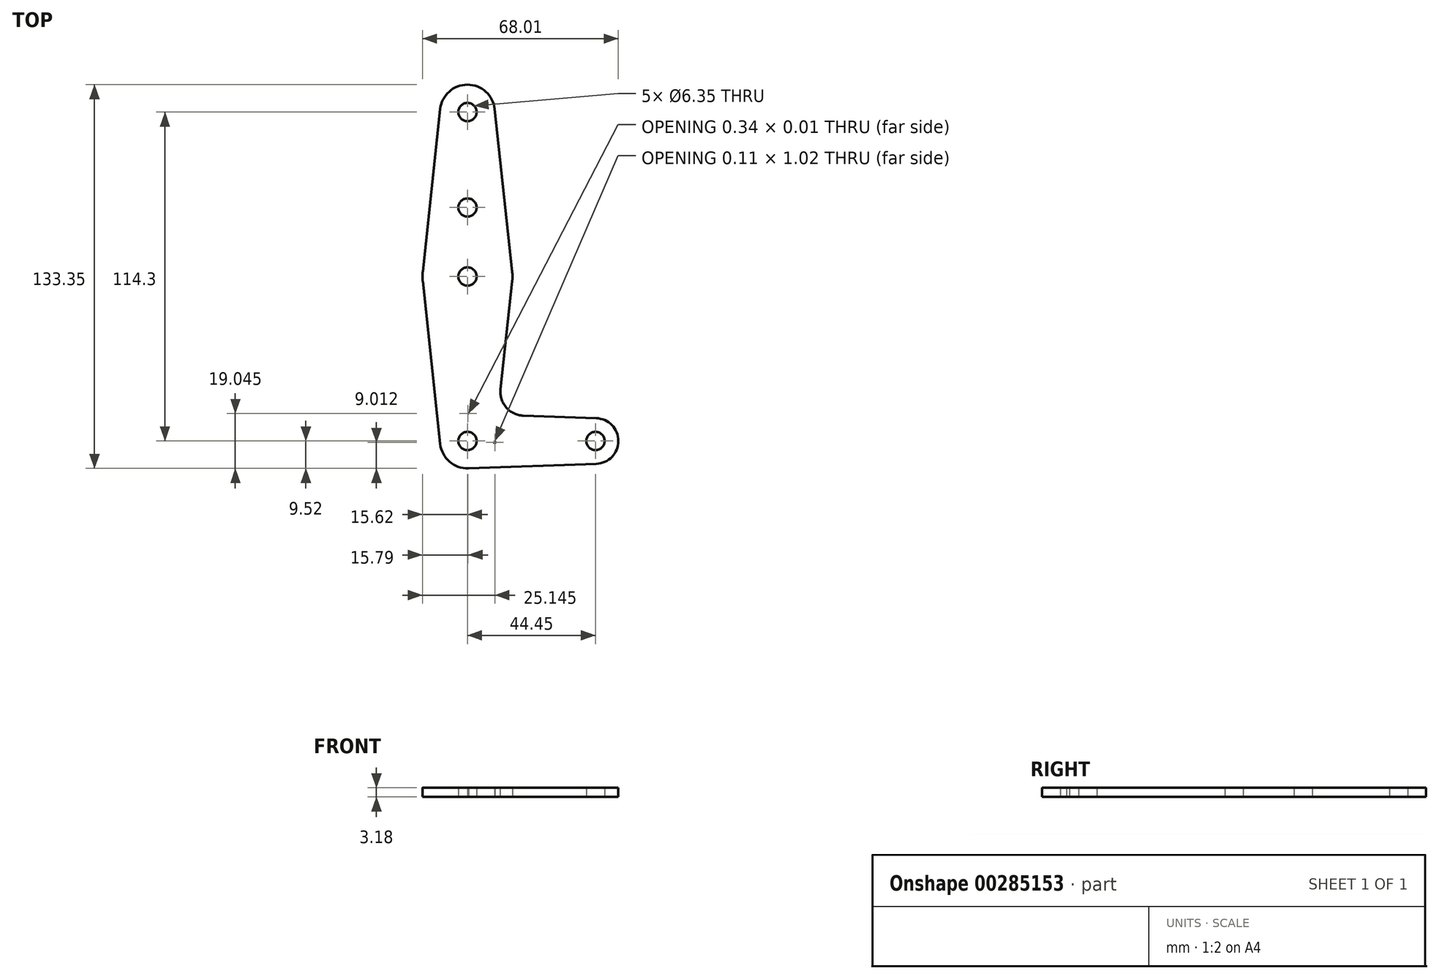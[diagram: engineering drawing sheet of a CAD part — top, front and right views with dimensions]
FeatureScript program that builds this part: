
annotation { "Feature Type Name" : "Feature", "Feature Type Description" : "" }
export const myFeature = defineFeature(function(context is Context, id is Id, definition is map)
    precondition{}
    {
        {
            var Q0;
            Q0=qCreatedBy(makeId("Top.planeOp"),FACE);
            var sketch = newSketch(context, id + "F0", { "sketchPlane" : qUnion([Q0])});
            skCircle(sketch, "E0", {"center": v(0, 0) * mm, "radius": 3.18 * mm});
            skCircle(sketch, "E1", {"center": v(0, 114.3) * mm, "radius": 3.18 * mm});
            skCircle(sketch, "E2", {"center": v(44.45, 0) * mm, "radius": 3.18 * mm});
            skLineSegment(sketch, "E3", {"start": v(0, 0) * mm, "end": v(44.45, 0) * mm});
            skLineSegment(sketch, "E4", {"start": v(0, 0) * mm, "end": v(0, 114.3) * mm});
            skCircle(sketch, "E5", {"center": v(0, 57.15) * mm, "radius": 3.18 * mm});
            skCircle(sketch, "E6", {"center": v(0, 81.14) * mm, "radius": 3.18 * mm});
            skCircle(sketch, "E7", {"center": v(0, 114.3) * mm, "radius": 9.53 * mm});
            skCircle(sketch, "E8", {"center": v(0, 57.15) * mm, "radius": 15.62 * mm});
            skCircle(sketch, "E9", {"center": v(0, 0) * mm, "radius": 9.53 * mm});
            skCircle(sketch, "E10", {"center": v(44.45, 0) * mm, "radius": 7.94 * mm});
            skLineSegment(sketch, "E11", {"start": v(-15.53, 58.82) * mm, "end": v(-9.47, 115.32) * mm});
            skLineSegment(sketch, "E12", {"start": v(9.47, 115.32) * mm, "end": v(15.53, 58.82) * mm});
            skLineSegment(sketch, "E13", {"start": v(-15.53, 55.48) * mm, "end": v(-9.47, -1.02) * mm});
            skLineSegment(sketch, "E14", {"start": v(15.53, 55.48) * mm, "end": v(9.47, -1.02) * mm});
            skLineSegment(sketch, "E15.trimOffspring", {"start": v(0, 9.53) * mm, "end": v(44.73, 7.93) * mm});
            skLineSegment(sketch, "E16", {"start": v(0.34, -9.52) * mm, "end": v(44.73, -7.93) * mm});
            skSolve(sketch);
        }
        {
            var Q0;
            {var subQ0=sQuery(id+"F0.wireOp",EDGE,"E11");Q0=makeQuery(id+"F0.imprint","IMPRINT",FACE,{"disambiguationData":[TD([[makeQuery(id+"F0.imprint","IMPRINT",EDGE,{"derivedFrom":subQ0}),-1.0]])]});}
            var Q1;
            {var subQ0=sQuery(id+"F0.wireOp",EDGE,"E12");Q1=makeQuery(id+"F0.imprint","IMPRINT",FACE,{"disambiguationData":[TD([[makeQuery(id+"F0.imprint","IMPRINT",EDGE,{"derivedFrom":subQ0}),-1.0]])]});}
            var Q2;
            Q2=makeQuery(id+"F0.imprint","IMPRINT",FACE,{"disambiguationData":[TD([[makeQuery(id+"F0.imprint","IMPRINT",EDGE,{"derivedFrom":sQuery(id+"F0.wireOp",EDGE,"E1")}),-1.0]])]});
            var Q3;
            {var subQ0=sQuery(id+"F0.wireOp",EDGE,"E13");Q3=makeQuery(id+"F0.imprint","IMPRINT",FACE,{"disambiguationData":[TD([[makeQuery(id+"F0.imprint","IMPRINT",EDGE,{"derivedFrom":subQ0}),1.0]])]});}
            var Q4;
            {var subQ3=sQuery(id+"F0.wireOp",EDGE,"E15.trimOffspring");var subQ5=sQuery(id+"F0.wireOp",EDGE,"E4");var subQ7=makeQuery(id+"F0.imprint","INTERSECT",VERTEX,{"derivedFrom":[subQ5,subQ3]});Q4=makeQuery(id+"F0.imprint","IMPRINT",FACE,{"disambiguationData":[TD([[makeQuery(id+"F0.imprint","IMPRINT",EDGE,{"disambiguationData":[TD([[subQ7,-1.0]])],"derivedFrom":subQ5}),-1.0]])]});}
            var Q5;
            {var subQ0=sQuery(id+"F0.wireOp",EDGE,"E8");var subQ2=sQuery(id+"F0.wireOp",EDGE,"E4");var subQ8=makeQuery(id+"F0.imprint","INTERSECT",VERTEX,{"disambiguationData":[OD(0.0)],"derivedFrom":[subQ2,subQ0]});Q5=makeQuery(id+"F0.imprint","IMPRINT",FACE,{"disambiguationData":[TD([[makeQuery(id+"F0.imprint","IMPRINT",EDGE,{"disambiguationData":[TD([[subQ8,-1.0]])],"derivedFrom":subQ2}),-1.0]])]});}
            var Q6;
            {var subQ0=sQuery(id+"F0.wireOp",EDGE,"E8");var subQ2=sQuery(id+"F0.wireOp",EDGE,"E4");var subQ7=makeQuery(id+"F0.imprint","INTERSECT",VERTEX,{"disambiguationData":[OD(0.0)],"derivedFrom":[subQ2,subQ0]});Q6=makeQuery(id+"F0.imprint","IMPRINT",FACE,{"disambiguationData":[TD([[makeQuery(id+"F0.imprint","IMPRINT",EDGE,{"disambiguationData":[TD([[subQ7,-1.0]])],"derivedFrom":subQ2}),1.0]])]});}
            var Q7;
            {var subQ4=sQuery(id+"F0.wireOp",EDGE,"E0");var subQ6=sQuery(id+"F0.wireOp",EDGE,"E3");var subQ7=makeQuery(id+"F0.imprint","INTERSECT",VERTEX,{"derivedFrom":[subQ4,subQ6]});Q7=makeQuery(id+"F0.imprint","IMPRINT",FACE,{"disambiguationData":[TD([[makeQuery(id+"F0.imprint","IMPRINT",EDGE,{"disambiguationData":[TD([[subQ7,1.0]])],"derivedFrom":subQ4}),-1.0]])]});}
            var Q8;
            {var subQ1=sQuery(id+"F0.wireOp",EDGE,"E3");var subQ5=sQuery(id+"F0.wireOp",EDGE,"E0");var subQ8=makeQuery(id+"F0.imprint","INTERSECT",VERTEX,{"derivedFrom":[subQ5,subQ1]});Q8=makeQuery(id+"F0.imprint","IMPRINT",FACE,{"disambiguationData":[TD([[makeQuery(id+"F0.imprint","IMPRINT",EDGE,{"disambiguationData":[TD([[subQ8,-1.0]])],"derivedFrom":subQ5}),-1.0]])]});}
            var Q9;
            {var subQ0=sQuery(id+"F0.wireOp",EDGE,"E9");var subQ1=sQuery(id+"F0.wireOp",EDGE,"E3");var subQ2=makeQuery(id+"F0.imprint","INTERSECT",VERTEX,{"derivedFrom":[subQ1,subQ0]});Q9=makeQuery(id+"F0.imprint","IMPRINT",FACE,{"disambiguationData":[TD([[makeQuery(id+"F0.imprint","IMPRINT",EDGE,{"disambiguationData":[TD([[subQ2,-1.0]])],"derivedFrom":subQ1}),1.0]])]});}
            var Q10;
            {var subQ0=sQuery(id+"F0.wireOp",EDGE,"E10");var subQ1=sQuery(id+"F0.wireOp",EDGE,"E3");var subQ2=makeQuery(id+"F0.imprint","INTERSECT",VERTEX,{"derivedFrom":[subQ1,subQ0]});Q10=makeQuery(id+"F0.imprint","IMPRINT",FACE,{"disambiguationData":[TD([[makeQuery(id+"F0.imprint","IMPRINT",EDGE,{"disambiguationData":[TD([[subQ2,1.0]])],"derivedFrom":subQ1}),1.0]])]});}
            var Q11;
            {var subQ0=sQuery(id+"F0.wireOp",EDGE,"E16");Q11=makeQuery(id+"F0.imprint","IMPRINT",FACE,{"disambiguationData":[TD([[makeQuery(id+"F0.imprint","IMPRINT",EDGE,{"derivedFrom":subQ0}),1.0]])]});}
            var Q12;
            Q12=makeQuery(id+"F0.imprint","IMPRINT",FACE,{"disambiguationData":[TD([[makeQuery(id+"F0.imprint","IMPRINT",EDGE,{"derivedFrom":sQuery(id+"F0.wireOp",EDGE,"E2")}),-1.0]])]});
            extrude(context, id + "F1", {"entities" : qUnion([Q0, Q1, Q2, Q3, Q4, Q5, Q6, Q7, Q8, Q9, Q10, Q11, Q12]), "depth" : 3.17 * mm});
        }
        {
            var Q0;
            Q0=makeQuery(id+"F1.opExtrude","SWEPT_EDGE",EDGE,{"disambiguationData":[OSD([sQuery(id+"F0.wireOp",EDGE,"E14"),sQuery(id+"F0.wireOp",EDGE,"E15.trimOffspring")])]});
            fillet(context, id + "F2", {"entities" : qUnion([Q0]), "radius" : 8.2 * mm, "tangentPropagation" : true, "allowEdgeOverflow" : false});
        }
    });
